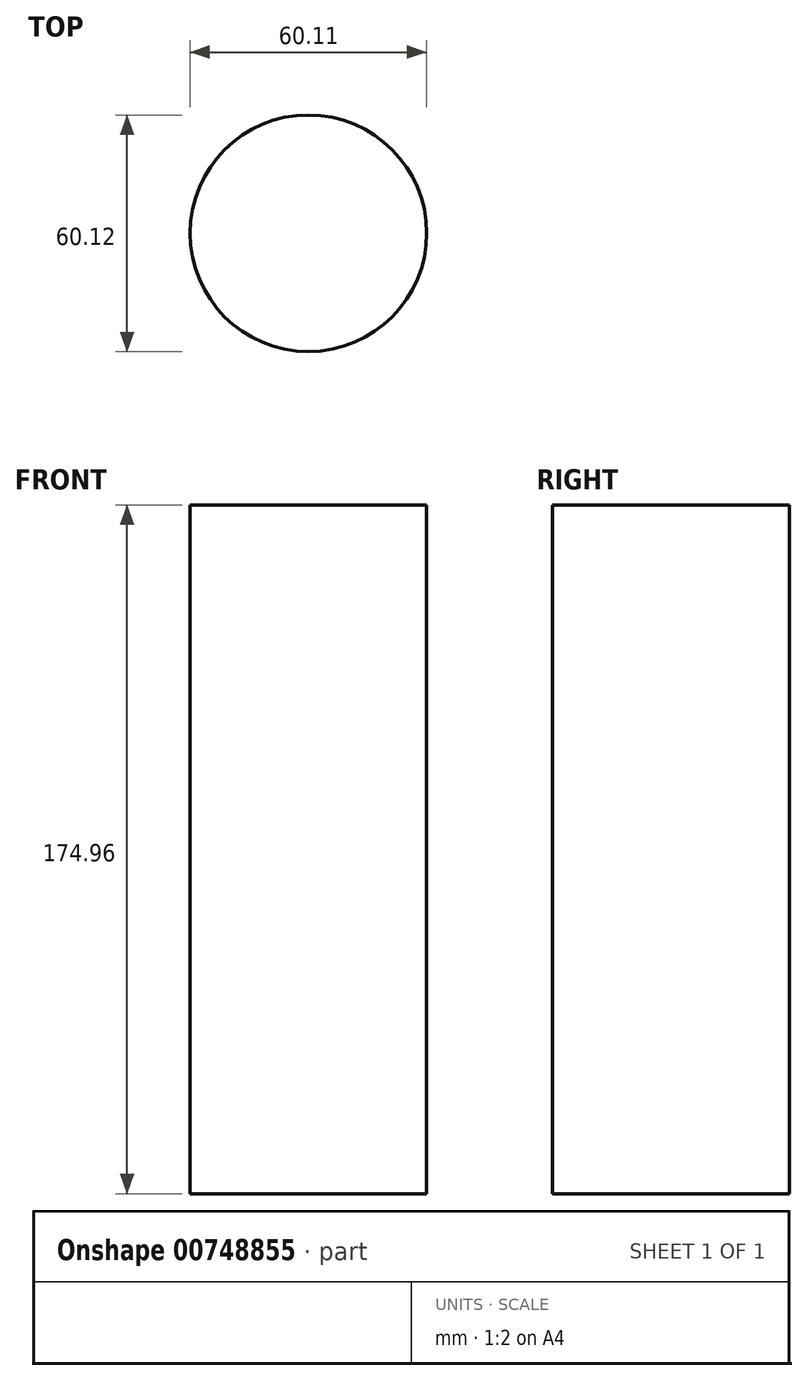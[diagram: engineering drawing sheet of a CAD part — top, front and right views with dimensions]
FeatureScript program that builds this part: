
annotation { "Feature Type Name" : "Feature", "Feature Type Description" : "" }
export const myFeature = defineFeature(function(context is Context, id is Id, definition is map)
    precondition{}
    {
        {
            var Q0;
            Q0=qCreatedBy(makeId("Top.planeOp"),FACE);
            var sketch = newSketch(context, id + "F0", { "sketchPlane" : qUnion([Q0])});
            skCircle(sketch, "E0", {"center": v(30.06, 0) * mm, "radius": 30.06 * mm});
            skSolve(sketch);
        }
        {
            var Q0;
            Q0 = qSketchRegion(id + "F0", true);
            extrude(context, id + "F1", {"entities" : qUnion([Q0]), "depth" : 174.96 * mm, "offsetDistance" : 25.4 * mm});
        }
    });
